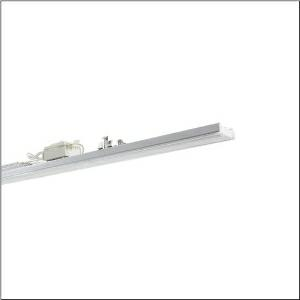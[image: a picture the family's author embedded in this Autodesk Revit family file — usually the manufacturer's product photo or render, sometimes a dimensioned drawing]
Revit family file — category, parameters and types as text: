
# Revit family: licross_11_recessed_extreme_ho_51te18dn4c5me
name_source: partatom
category: Lighting Fixtures
units: mm (PartAtom-declared; Revit-internal decimal feet)

## family parameters
Cut with Voids When Loaded = No
Host = Face
Light Source = No
Part Type = Normal
Room Calculation Point = No
Round Connector Dimension = Use Diameter
Shared = No

## types (1)
- --- (1 x LED, 12830 lm, 70.5 W, 4000K)
    Apparent Load = 71 VA
    CIE Flux Codes = 78 94 99 100 100
    Color Rendering = 80
    Color Temperature = 4000K
    Default Elevation = 1800 mm
    Description = Licross 11 Recessed extreme HO, luminaire insert, of sheet steel, galvanised, coil coated, white, length: 1.500mm, width: 66mm, height: 67mm, LED rated luminous flux: 12.830lm, light colour: 840, SDCM (Standard Deviation of Colour Matching)MacAdam ≤ 2 SDCM (initial), control gear: DALI 2, with plug, 5-pole, with phase selection, mains connection: 220..240V, AC, 50/60Hz, rated input power: 71W, internal wiring halogen-free, primary light control with lens, of plastic, primary optical cover: cover, of PMMA, light emission: direct distribution, primary light characteristic: symmetric, protection rating (complete): IP54, insulation class (complete): insulation class I (protective earthing), certification: CE, ENEC, VDE, UKCA, protection symbol: D if used in an environment with non-conductive dust loads with corresponding accessories, impact resistance: IK06, permissible ambient temperature for indoor applications: -25..+45°C, corresponds to IFS (International Featured Standards) requirements for safety and quality in the food industry, reducing of maximum allowable ambient temperature of 5°C with ceiling mounting, LABS conformity tested according to VDMA 24364:2018-05, The light source and the operating device comply with the requirements of the Ecodesign Regulation (EU) 2019/2020 and are replaceable in accordance with this regulation, packaging unit: 1 piece
    Height = 58 mm
    Lamp = 1 x LED
    Lamp Light Flux = 12830 lm
    Lamp Power = 70.5 W
    Lamp count = 1
    Length = 1500 mm
    Luminous efficacy = 182 lm/W
    Manufacturer = Siteco
    ModVariant = No
    Model = 51TE18DN4C5ME
    Mounting Place = Ceiling
    Mounting Type = Pendant
    Number of Poles = 1
    OnlyDefault = Yes
    Power Factor = 1
    Product Name = Licross 11 Recessed extreme HO
    Product group = luminaire insert | ceiling pendant
    ProductGroupID = 901
    Protection Class = Protection class I
    Protection Degree = IP 54
    RLX_Detail_Level = 1
    RLX_Emergency_Light_Flux = 0 lm
    RLX_Emergency_Type = 0
    RLX_Emergency_Type_DB = No
    RlxData = <blob elided: 24949 chars, md5=615b9db8>
    Socket = socket
    Standby Power = 0 W
    System Light Flux = 12830 lm
    System Power = 71 W
    Type Comments = factory setting: luminous flux: 100 % | dim-lin: 254 | 479 mA
    Type Image = l_1296930.jpg
    URL = http://relux.com
    VarID = @adj_093709
    Voltage = 0 V
    Weight = 0.00 kg
    Width = 66 mm

## geometry (parser evidence)
native form markers: Blend x4, Sweep x10
no freeform markers — native parametric forms only
